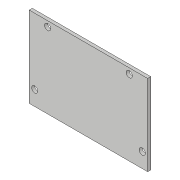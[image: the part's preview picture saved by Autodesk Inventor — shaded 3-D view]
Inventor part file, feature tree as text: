
AUTODESK INVENTOR PART (.ipt)
format: ipt  version: 2018.3 (Build 223284000, 284)  size: 95,744 bytes
history: native  units: in
note: dims shown in document units (in); Inventor stores cm internally (conversion verified against a paired STEP export)
features: extrude x2, sketch x2
ambient origin geometry x8: Origin, YZ Plane, XZ Plane, XY Plane, X Axis, Y Axis, Z Axis, Center Point
bodies: Solid1 (feature_tree)
feature tree (4):
  extrude  "Extrusion1"  Depth=2.3823in
  extrude  "Extrusion2"  Depth=0.0625in
  sketch  "Sketch1"  dims[d0=1.625in d1=2.3823in]
  sketch  "Sketch2"  dims[d2=0.0625in d3=0.0in d13=0.125in d14=0.1105in d15=0.2975in d16=0.125in d17=0.2975in d18=0.1105in d19=0.125in d20=0.371in d21=0.371in d22=0.125in d23=0.1105in d24=0.1105in d25=0.0625in d26=0.0in]
